# Revit family: Indirect-Water-Heater_AO_Smith-IT-2500_B
name_source: partatom
category: Mechanical Equipment
revit_build: Autodesk Revit 2016 (Build: 20170117_1200(x64)
units: mm (PartAtom-declared; Revit-internal decimal feet)

## family parameters
Always vertical = Yes
Cut with Voids When Loaded = No
OmniClass Number = 23.75.00.00
OmniClass Title = Climate Control (HVAC)
Part Type = Normal
Room Calculation Point = No
Round Connector Dimension = Use Radius
Shared = No
Work Plane-Based = No

## types (1)
- Indirect-Water-Heater_AO_Smith-IT-2500_B
    1er Entretien (check-up) = 3 mois après l'installation
    2ème Entretien (Entretien Général) = 12 mois après l'installation
    Assembly Code = D3010
    BIM Content Developer = CAD & Company
    BIM Content Developer URL = http://www.cadcompany.nl
    Capacité - Cuve = 2550 m³
    Capacité - Échangeur Inférieur = 45 m³
    Charge Maximale au Sol = 3126.00 kg
    Description = Cuve Indirects Fournis d’un Échangeur
    Destination / Pays = Belgique
    Diamètre (avec Isolation) = 1600 mm  [stored 5.24934 ft]
    Diamètre (sans Isolation) = 1400 mm  [stored 4.59318 ft]
    Débit de vidage en Continu à ΔT = 28°C = 4454
    Débit de vidage en Continu à ΔT = 44°C = 2834
    Débit de vidage en Continu à ΔT = 50°C = 2494
    Débit de vidage en Continu à ΔT = 55°C = 2267
    Débit de vidage en Continu à ΔT = 70°C = 1781
    Débit de vidage à ΔT = 28°C après 120 min. = 10699.0 L
    Débit de vidage à ΔT = 28°C après 30 min. = 4018.0 L
    Débit de vidage à ΔT = 28°C après 60 min. = 6245.0 L
    Débit de vidage à ΔT = 28°C après 90 min. = 8472.0 L
    Débit de vidage à ΔT = 44°C après 120 min. = 6808.0 L
    Débit de vidage à ΔT = 44°C après 30 min. = 2557.0 L
    Débit de vidage à ΔT = 44°C après 60 min. = 3974.0 L
    Débit de vidage à ΔT = 44°C après 90 min. = 5391.0 L
    Débit de vidage à ΔT = 50°C après 120 min. = 5991.0 L
    Débit de vidage à ΔT = 50°C après 30 min. = 2250.0 L
    Débit de vidage à ΔT = 50°C après 60 min. = 3497.0 L
    Débit de vidage à ΔT = 50°C après 90 min. = 4744.0 L
    Débit de vidage à ΔT = 55°C après 120 min. = 5447.0 L
    Débit de vidage à ΔT = 55°C après 30 min. = 2046.0 L
    Débit de vidage à ΔT = 55°C après 60 min. = 3179.0 L
    Débit de vidage à ΔT = 55°C après 90 min. = 4313.0 L
    Débit de vidage à ΔT = 70°C après 120 min. = 4279.0 L
    Débit de vidage à ΔT = 70°C après 30 min. = 1607.0 L
    Débit de vidage à ΔT = 70°C après 60 min. = 2498.0 L
    Débit de vidage à ΔT = 70°C après 90 min. = 3389.0 L
    Débit à 80ºC/60ºC - Échangeur Inférieur = 6871
    Epaisseur d'Isolation = 100 mm  [stored 0.328084 ft]
    Fabricant No. = E 7110
    Garantie Pièces = 12 mois
    Garantie sur la Cuve = 36 mois
    Guide de Produit = https://www.aosmithinternational.com
    Hauteur (avec Isolation) = 2045 mm  [stored 6.70932 ft]
    Hauteur (sans Isolation) = 2045 mm  [stored 6.70932 ft]
    Hauteur d'Emballage = 2120 mm  [stored 6.95538 ft]
    Hauteur de l'Alimentation en eau Froide = 185 mm  [stored 0.606955 ft]
    Hauteur de la Sortie d'eau Chaude = 2045 mm  [stored 6.70932 ft]
    Largeur d'Emballage = 1498 mm  [stored 4.9147 ft]
    Manufacturer = A.O. Smith Water Products Company b.v.
    Max. Température de l'eau - Réservoir = 85 °C
    Model = IT 2500 B
    Niveau du Son = 0
    Nombre de modèle du produit (EAN) = 8717449273385
    Perte de Pression à 80ºC/60ºC - Échangeur Inférieur = 695000.0 Pa
    Pertes en Veille = 0 W
    Pertes en Veille - tous les jours (24h) = 0
    Poids de Transport = 686.00 kg
    Poids à vide = 576.00 kg
    Pression de Service Maximale - Réservoir = 80000.0 Pa
    Pression de Service Maximale - Échangeur Inférieur = 60000.0 Pa
    Production Nominale - Échangeur Inférieur = 156000 W
    Profondeur d'Emballage = 1680 mm  [stored 5.51181 ft]
    Raccord d'Alimentation en Eau Froide = 2"
    Raccord de Sortie d'Eau Chaude = 2"
    Raccord de la Soupape de Vidange = 1"
    Spécifications du Produit = https://www.aosmithinternational.com
    Surface d'Échange de Chaleur - Échangeur Inférieur = 6 m²
    Temps de réchauffement à ΔT = 28°C = 14
    Temps de réchauffement à ΔT = 44°C = 21
    Temps de réchauffement à ΔT = 50°C = 24
    Temps de réchauffement à ΔT = 55°C = 27
    Temps de réchauffement à ΔT = 70°C = 34
    Température Maximale - Échangeur Inférieur = 90 °C
    Type d'Emballage = Plastique et Bois
    URL = https://www.aosmithinternational.com
    Workspace Diameter = 2600 mm  [stored 8.53018 ft]
    Workspace Height = 3045 mm
    espace de travail = 1250 mm  [stored 4.10105 ft]
    l'Intervalle d'Entretien = 12 mois

note: [stored X ft] marks values corroborated as IEEE doubles in the binary element streams (Revit-internal decimal feet)

## geometry (parser evidence)
native form markers: Blend x2, Sweep x20
no freeform markers — native parametric forms only
